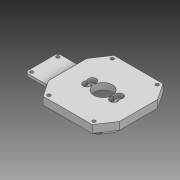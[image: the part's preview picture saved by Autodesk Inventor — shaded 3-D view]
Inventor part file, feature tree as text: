
AUTODESK INVENTOR PART (.ipt)
format: ipt  version: 2018 (Build 220112000, 112)  size: 807,936 bytes
history: native  units: mm
features: sketch x17, extrude x16, mirror x5, chamfer x2, other x2, pattern_circular x2, projected_geometry x2, fillet x1
ambient origin geometry x8: Origin, YZ Plane, XZ Plane, XY Plane, X Axis, Y Axis, Z Axis, Center Point
bodies: Body1 (feature_tree)
feature tree (47):
  extrude  "押し出し2"  Depth=12.0mm TaperAngle=0.0deg
  extrude  "押し出し3"  Depth=17.0mm
  extrude  "押し出し4"  Depth=10.0mm TaperAngle=0.0deg
  extrude  "押し出し5"  Depth=36.5mm
  extrude  "押し出し6"  Depth=6.0mm TaperAngle=0.0deg
  chamfer  "面取り1"  Distance=25.0mm
  extrude  "押し出し7"  Depth=3.0mm
  extrude  "押し出し8"  Depth=3.0mm
  mirror  "ミラー1"
  other  "作業平面1"
  extrude  "押し出し9"  Depth=2.5mm
  extrude  "押し出し10"  Depth=5.0mm TaperAngle=0.0deg
  pattern_circular  "円形状パターン1"  [2 undecoded]
  sketch  "スケッチ12"
  extrude  "押し出し12"  Depth=2.0mm
  pattern_circular  "円形状パターン2"  [2 undecoded]
  extrude  "押し出し11"  Depth=2.0mm
  extrude  "押し出し13"  Depth=4.0mm TaperAngle=0.0deg
  extrude  "押し出し14"  Depth=5.0mm TaperAngle=45.0deg
  mirror  "ミラー3"
  extrude  "押し出し15"  Depth=2.0mm
  extrude  "押し出し16"  Depth=5.0mm
  fillet  "フィレット1"  Radius=7.0mm
  mirror  "ミラー4"
  chamfer  "面取り3"  Angle=45.0deg  [1 undecoded]
  extrude  "押し出し17"  Depth=3.0mm
  mirror  "ミラー5"
  mirror  "ミラー6"
  other  "エンボス1"
  sketch  "スケッチ2"
  sketch  "スケッチ3"
  sketch  "スケッチ4"
  sketch  "スケッチ5"
  sketch  "スケッチ6"
  sketch  "スケッチ7"
  projected_geometry  "投影ループ1"
  sketch  "スケッチ8"
  sketch  "スケッチ9"
  sketch  "スケッチ10"
  projected_geometry  "投影ループ2"
  sketch  "スケッチ11"
  sketch  "スケッチ13"
  sketch  "スケッチ14"
  sketch  "スケッチ15"
  sketch  "スケッチ16"
  sketch  "スケッチ17"
  sketch  "スケッチ18"
note: 5 required parameter values undecoded (feature->parameter linkage not recoverable at this tier; creation-order binding heuristic only, values carry confidence <= 0.55)
